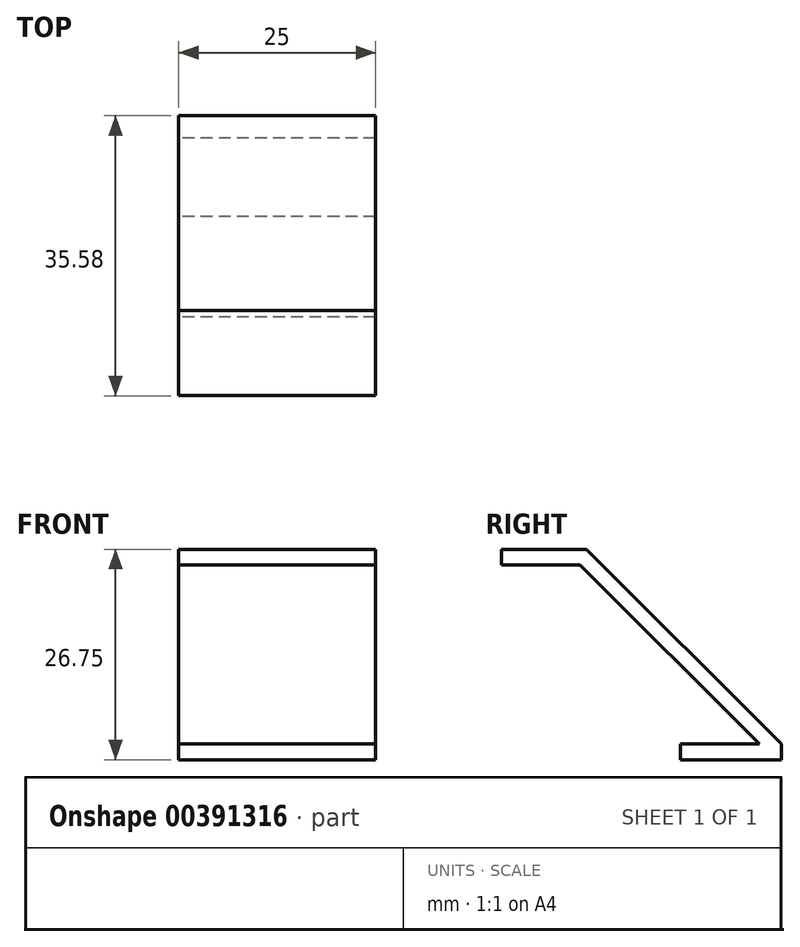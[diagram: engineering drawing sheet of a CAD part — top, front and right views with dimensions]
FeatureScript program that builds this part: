
annotation { "Feature Type Name" : "Feature", "Feature Type Description" : "" }
export const myFeature = defineFeature(function(context is Context, id is Id, definition is map)
    precondition{}
    {
        {
            var Q0;
            Q0=qCreatedBy(makeId("Right.planeOp"),FACE);
            var sketch = newSketch(context, id + "F0", { "sketchPlane" : qUnion([Q0])});
            skLineSegment(sketch, "E0", {"start": v(-39.75, 24.75) * mm, "end": v(-49.75, 24.75) * mm});
            skLineSegment(sketch, "E1", {"start": v(-49.75, 24.75) * mm, "end": v(-49.75, 26.75) * mm});
            skLineSegment(sketch, "E2", {"start": v(-49.75, 26.75) * mm, "end": v(-38.92, 26.75) * mm});
            skLineSegment(sketch, "E3", {"start": v(-38.92, 26.75) * mm, "end": v(-14.17, 2) * mm});
            skLineSegment(sketch, "E4", {"start": v(-14.17, 2) * mm, "end": v(-14.17, 0) * mm});
            skLineSegment(sketch, "E5", {"start": v(-14.17, 0) * mm, "end": v(-27, 0) * mm});
            skLineSegment(sketch, "E6", {"start": v(-27, 0) * mm, "end": v(-27, 2) * mm});
            skLineSegment(sketch, "E7", {"start": v(-27, 2) * mm, "end": v(-17, 2) * mm});
            skLineSegment(sketch, "E8", {"start": v(-17, 2) * mm, "end": v(-39.75, 24.75) * mm});
            skSolve(sketch);
        }
        {
            var Q0;
            Q0=makeQuery(id+"F0.imprint","IMPRINT",FACE,{"disambiguationData":[TD([[makeQuery(id+"F0.imprint","IMPRINT",EDGE,{"derivedFrom":sQuery(id+"F0.wireOp",EDGE,"E0")}),-1.0]])]});
            extrude(context, id + "F1", {"entities" : qUnion([Q0]), "depth" : 25 * mm, "offsetDistance" : 25 * mm});
        }
    });
